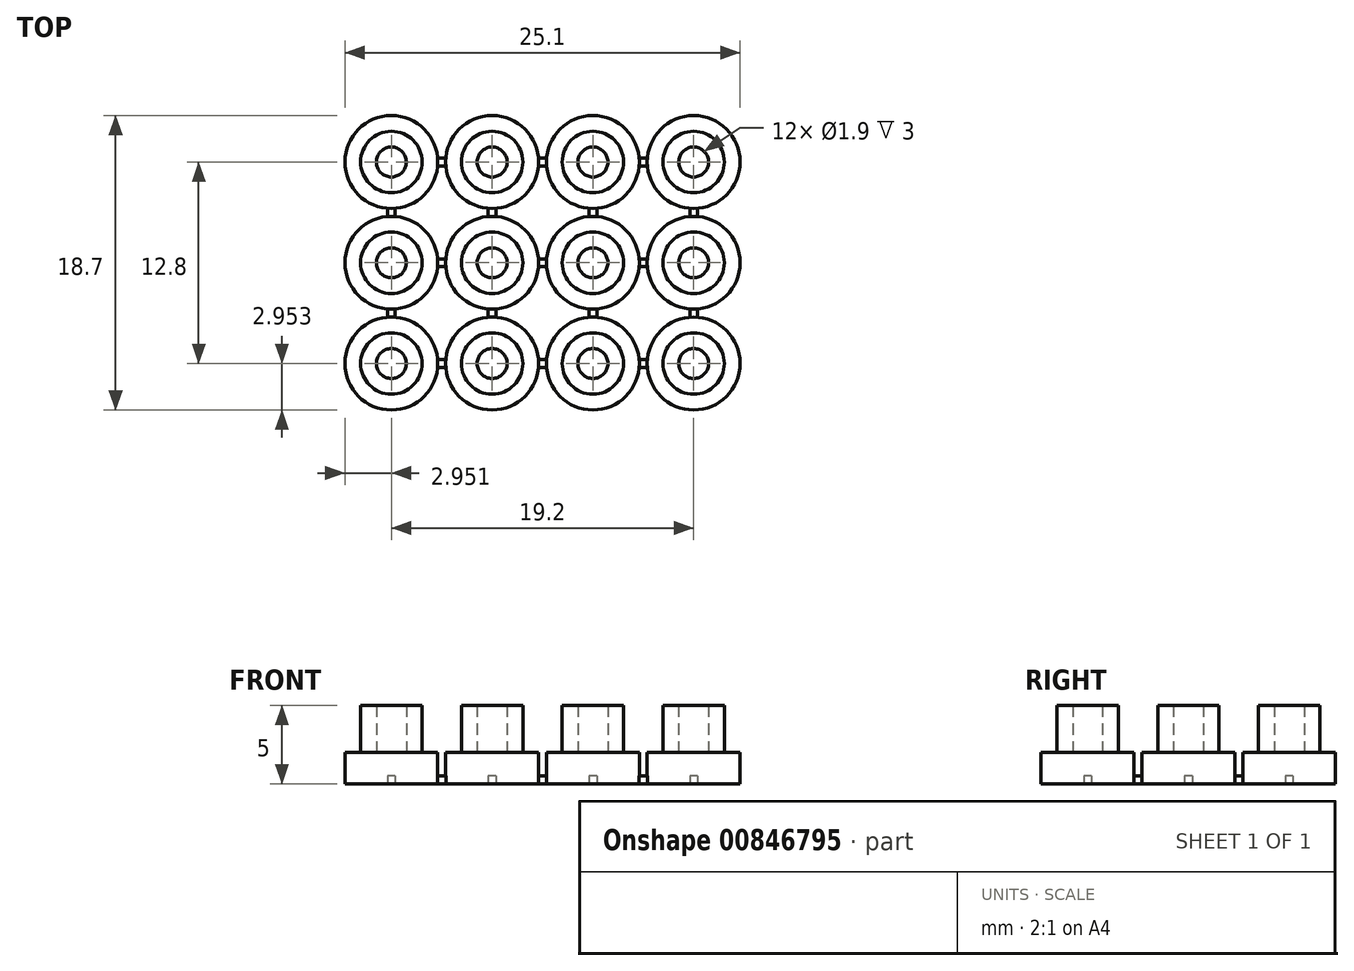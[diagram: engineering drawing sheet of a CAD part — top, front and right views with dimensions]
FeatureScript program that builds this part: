
annotation { "Feature Type Name" : "Feature", "Feature Type Description" : "" }
export const myFeature = defineFeature(function(context is Context, id is Id, definition is map)
    precondition{}
    {
        {
            var Q0;
            Q0=qCreatedBy(makeId("Top.planeOp"),FACE);
            var sketch = newSketch(context, id + "F0", { "sketchPlane" : qUnion([Q0])});
            skCircle(sketch, "E0", {"center": v(-49.05, 28.15) * mm, "radius": 0.95 * mm});
            skCircle(sketch, "E1", {"center": v(-49.05, 28.15) * mm, "radius": 1.95 * mm});
            skCircle(sketch, "E2", {"center": v(-49.05, 28.15) * mm, "radius": 2.95 * mm});
            skCircle(sketch, "E3.0.1.0", {"center": v(-49.05, 34.55) * mm, "radius": 2.95 * mm});
            skCircle(sketch, "E3.0.1.1", {"center": v(-49.05, 34.55) * mm, "radius": 1.95 * mm});
            skCircle(sketch, "E3.0.1.2", {"center": v(-49.05, 34.55) * mm, "radius": 0.95 * mm});
            skCircle(sketch, "E3.0.2.0", {"center": v(-49.05, 40.95) * mm, "radius": 2.95 * mm});
            skCircle(sketch, "E3.0.2.1", {"center": v(-49.05, 40.95) * mm, "radius": 1.95 * mm});
            skCircle(sketch, "E3.0.2.2", {"center": v(-49.05, 40.95) * mm, "radius": 0.95 * mm});
            skCircle(sketch, "E3.1.0.0", {"center": v(-42.65, 28.15) * mm, "radius": 2.95 * mm});
            skCircle(sketch, "E3.1.0.1", {"center": v(-42.65, 28.15) * mm, "radius": 1.95 * mm});
            skCircle(sketch, "E3.1.0.2", {"center": v(-42.65, 28.15) * mm, "radius": 0.95 * mm});
            skCircle(sketch, "E3.1.1.0", {"center": v(-42.65, 34.55) * mm, "radius": 2.95 * mm});
            skCircle(sketch, "E3.1.1.1", {"center": v(-42.65, 34.55) * mm, "radius": 1.95 * mm});
            skCircle(sketch, "E3.1.1.2", {"center": v(-42.65, 34.55) * mm, "radius": 0.95 * mm});
            skCircle(sketch, "E3.1.2.0", {"center": v(-42.65, 40.95) * mm, "radius": 2.95 * mm});
            skCircle(sketch, "E3.1.2.1", {"center": v(-42.65, 40.95) * mm, "radius": 1.95 * mm});
            skCircle(sketch, "E3.1.2.2", {"center": v(-42.65, 40.95) * mm, "radius": 0.95 * mm});
            skCircle(sketch, "E3.2.0.0", {"center": v(-36.25, 28.15) * mm, "radius": 2.95 * mm});
            skCircle(sketch, "E3.2.0.1", {"center": v(-36.25, 28.15) * mm, "radius": 1.95 * mm});
            skCircle(sketch, "E3.2.0.2", {"center": v(-36.25, 28.15) * mm, "radius": 0.95 * mm});
            skCircle(sketch, "E3.2.1.0", {"center": v(-36.25, 34.55) * mm, "radius": 2.95 * mm});
            skCircle(sketch, "E3.2.1.1", {"center": v(-36.25, 34.55) * mm, "radius": 1.95 * mm});
            skCircle(sketch, "E3.2.1.2", {"center": v(-36.25, 34.55) * mm, "radius": 0.95 * mm});
            skCircle(sketch, "E3.2.2.0", {"center": v(-36.25, 40.95) * mm, "radius": 2.95 * mm});
            skCircle(sketch, "E3.2.2.1", {"center": v(-36.25, 40.95) * mm, "radius": 1.95 * mm});
            skCircle(sketch, "E3.2.2.2", {"center": v(-36.25, 40.95) * mm, "radius": 0.95 * mm});
            skCircle(sketch, "E3.3.0.0", {"center": v(-29.85, 28.15) * mm, "radius": 2.95 * mm});
            skCircle(sketch, "E3.3.0.1", {"center": v(-29.85, 28.15) * mm, "radius": 1.95 * mm});
            skCircle(sketch, "E3.3.0.2", {"center": v(-29.85, 28.15) * mm, "radius": 0.95 * mm});
            skCircle(sketch, "E3.3.1.0", {"center": v(-29.85, 34.55) * mm, "radius": 2.95 * mm});
            skCircle(sketch, "E3.3.1.1", {"center": v(-29.85, 34.55) * mm, "radius": 1.95 * mm});
            skCircle(sketch, "E3.3.1.2", {"center": v(-29.85, 34.55) * mm, "radius": 0.95 * mm});
            skCircle(sketch, "E3.3.2.0", {"center": v(-29.85, 40.95) * mm, "radius": 2.95 * mm});
            skCircle(sketch, "E3.3.2.1", {"center": v(-29.85, 40.95) * mm, "radius": 1.95 * mm});
            skCircle(sketch, "E3.3.2.2", {"center": v(-29.85, 40.95) * mm, "radius": 0.95 * mm});
            skLineSegment(sketch, "E3.direction1", {"start": v(-49.05, 28.15) * mm, "end": v(-42.65, 28.15) * mm, "construction": true});
            skLineSegment(sketch, "E3.direction2", {"start": v(-49.05, 28.15) * mm, "end": v(-49.05, 34.55) * mm, "construction": true});
            skPoint(sketch, "E4", {"position": v(-49.05, 31.35) * mm});
            skPoint(sketch, "E5", {"position": v(-45.85, 28.15) * mm});
            skLineSegment(sketch, "E6.left", {"start": v(-48.8, 31.1) * mm, "end": v(-48.8, 31.61) * mm});
            skLineSegment(sketch, "E6.right", {"start": v(-49.3, 31.1) * mm, "end": v(-49.3, 31.61) * mm});
            skLineSegment(sketch, "E7.0.1.0", {"start": v(-49.3, 37.5) * mm, "end": v(-49.3, 38.01) * mm});
            skLineSegment(sketch, "E7.0.1.1", {"start": v(-48.8, 37.5) * mm, "end": v(-48.8, 38.01) * mm});
            skLineSegment(sketch, "E7.1.0.0", {"start": v(-42.9, 31.1) * mm, "end": v(-42.9, 31.61) * mm});
            skLineSegment(sketch, "E7.1.0.1", {"start": v(-42.4, 31.1) * mm, "end": v(-42.4, 31.61) * mm});
            skLineSegment(sketch, "E7.1.1.0", {"start": v(-42.9, 37.5) * mm, "end": v(-42.9, 38.01) * mm});
            skLineSegment(sketch, "E7.1.1.1", {"start": v(-42.4, 37.5) * mm, "end": v(-42.4, 38.01) * mm});
            skLineSegment(sketch, "E7.2.0.0", {"start": v(-36.5, 31.1) * mm, "end": v(-36.5, 31.61) * mm});
            skLineSegment(sketch, "E7.2.0.1", {"start": v(-36, 31.1) * mm, "end": v(-36, 31.61) * mm});
            skLineSegment(sketch, "E7.2.1.0", {"start": v(-36.5, 37.5) * mm, "end": v(-36.5, 38.01) * mm});
            skLineSegment(sketch, "E7.2.1.1", {"start": v(-36, 37.5) * mm, "end": v(-36, 38.01) * mm});
            skLineSegment(sketch, "E7.3.0.0", {"start": v(-30.1, 31.1) * mm, "end": v(-30.1, 31.61) * mm});
            skLineSegment(sketch, "E7.3.0.1", {"start": v(-29.6, 31.1) * mm, "end": v(-29.6, 31.61) * mm});
            skLineSegment(sketch, "E7.3.1.0", {"start": v(-30.1, 37.5) * mm, "end": v(-30.1, 38.01) * mm});
            skLineSegment(sketch, "E7.3.1.1", {"start": v(-29.6, 37.5) * mm, "end": v(-29.6, 38.01) * mm});
            skLineSegment(sketch, "E7.direction1", {"start": v(-49.3, 31.1) * mm, "end": v(-42.9, 31.1) * mm, "construction": true});
            skLineSegment(sketch, "E7.direction2", {"start": v(-49.3, 31.1) * mm, "end": v(-49.3, 37.5) * mm, "construction": true});
            skLineSegment(sketch, "E8.bottom", {"start": v(-45.59, 28.4) * mm, "end": v(-46.1, 28.4) * mm});
            skLineSegment(sketch, "E8.top", {"start": v(-45.59, 27.9) * mm, "end": v(-46.1, 27.9) * mm});
            skLineSegment(sketch, "E9.0.1.0", {"start": v(-45.59, 34.8) * mm, "end": v(-46.1, 34.8) * mm});
            skLineSegment(sketch, "E9.0.1.1", {"start": v(-45.59, 34.3) * mm, "end": v(-46.1, 34.3) * mm});
            skLineSegment(sketch, "E9.0.2.0", {"start": v(-45.59, 41.2) * mm, "end": v(-46.1, 41.2) * mm});
            skLineSegment(sketch, "E9.0.2.1", {"start": v(-45.59, 40.7) * mm, "end": v(-46.1, 40.7) * mm});
            skLineSegment(sketch, "E9.1.0.0", {"start": v(-39.19, 28.4) * mm, "end": v(-39.7, 28.4) * mm});
            skLineSegment(sketch, "E9.1.0.1", {"start": v(-39.19, 27.9) * mm, "end": v(-39.7, 27.9) * mm});
            skLineSegment(sketch, "E9.1.1.0", {"start": v(-39.19, 34.8) * mm, "end": v(-39.7, 34.8) * mm});
            skLineSegment(sketch, "E9.1.1.1", {"start": v(-39.19, 34.3) * mm, "end": v(-39.7, 34.3) * mm});
            skLineSegment(sketch, "E9.1.2.0", {"start": v(-39.19, 41.2) * mm, "end": v(-39.7, 41.2) * mm});
            skLineSegment(sketch, "E9.1.2.1", {"start": v(-39.19, 40.7) * mm, "end": v(-39.7, 40.7) * mm});
            skLineSegment(sketch, "E9.2.0.0", {"start": v(-32.79, 28.4) * mm, "end": v(-33.3, 28.4) * mm});
            skLineSegment(sketch, "E9.2.0.1", {"start": v(-32.79, 27.9) * mm, "end": v(-33.3, 27.9) * mm});
            skLineSegment(sketch, "E9.2.1.0", {"start": v(-32.79, 34.8) * mm, "end": v(-33.3, 34.8) * mm});
            skLineSegment(sketch, "E9.2.1.1", {"start": v(-32.79, 34.3) * mm, "end": v(-33.3, 34.3) * mm});
            skLineSegment(sketch, "E9.2.2.0", {"start": v(-32.79, 41.2) * mm, "end": v(-33.3, 41.2) * mm});
            skLineSegment(sketch, "E9.2.2.1", {"start": v(-32.79, 40.7) * mm, "end": v(-33.3, 40.7) * mm});
            skLineSegment(sketch, "E9.direction1", {"start": v(-46.1, 27.9) * mm, "end": v(-39.7, 27.9) * mm, "construction": true});
            skLineSegment(sketch, "E9.direction2", {"start": v(-46.1, 27.9) * mm, "end": v(-46.1, 34.3) * mm, "construction": true});
            skSolve(sketch);
        }
        {
            var Q0;
            Q0=makeQuery(id+"F0.imprint","IMPRINT",FACE,{"disambiguationData":[TD([[makeQuery(id+"F0.imprint","IMPRINT",EDGE,{"derivedFrom":sQuery(id+"F0.wireOp",EDGE,"E0")}),-1.0]])]});
            var Q1;
            Q1=makeQuery(id+"F0.imprint","IMPRINT",FACE,{"disambiguationData":[TD([[makeQuery(id+"F0.imprint","IMPRINT",EDGE,{"derivedFrom":sQuery(id+"F0.wireOp",EDGE,"E3.1.0.1")}),1.0]])]});
            var Q2;
            Q2=makeQuery(id+"F0.imprint","IMPRINT",FACE,{"disambiguationData":[TD([[makeQuery(id+"F0.imprint","IMPRINT",EDGE,{"derivedFrom":sQuery(id+"F0.wireOp",EDGE,"E3.2.0.1")}),1.0]])]});
            var Q3;
            Q3=makeQuery(id+"F0.imprint","IMPRINT",FACE,{"disambiguationData":[TD([[makeQuery(id+"F0.imprint","IMPRINT",EDGE,{"derivedFrom":sQuery(id+"F0.wireOp",EDGE,"E3.0.1.1")}),1.0]])]});
            var Q4;
            Q4=makeQuery(id+"F0.imprint","IMPRINT",FACE,{"disambiguationData":[TD([[makeQuery(id+"F0.imprint","IMPRINT",EDGE,{"derivedFrom":sQuery(id+"F0.wireOp",EDGE,"E3.0.2.1")}),1.0]])]});
            var Q5;
            Q5=makeQuery(id+"F0.imprint","IMPRINT",FACE,{"disambiguationData":[TD([[makeQuery(id+"F0.imprint","IMPRINT",EDGE,{"derivedFrom":sQuery(id+"F0.wireOp",EDGE,"E3.1.1.1")}),1.0]])]});
            var Q6;
            Q6=makeQuery(id+"F0.imprint","IMPRINT",FACE,{"disambiguationData":[TD([[makeQuery(id+"F0.imprint","IMPRINT",EDGE,{"derivedFrom":sQuery(id+"F0.wireOp",EDGE,"E3.1.2.1")}),1.0]])]});
            var Q7;
            Q7=makeQuery(id+"F0.imprint","IMPRINT",FACE,{"disambiguationData":[TD([[makeQuery(id+"F0.imprint","IMPRINT",EDGE,{"derivedFrom":sQuery(id+"F0.wireOp",EDGE,"E3.2.1.1")}),1.0]])]});
            var Q8;
            Q8=makeQuery(id+"F0.imprint","IMPRINT",FACE,{"disambiguationData":[TD([[makeQuery(id+"F0.imprint","IMPRINT",EDGE,{"derivedFrom":sQuery(id+"F0.wireOp",EDGE,"E3.2.2.1")}),1.0]])]});
            var Q9;
            Q9=makeQuery(id+"F0.imprint","IMPRINT",FACE,{"disambiguationData":[TD([[makeQuery(id+"F0.imprint","IMPRINT",EDGE,{"derivedFrom":sQuery(id+"F0.wireOp",EDGE,"E3.3.2.1")}),1.0]])]});
            var Q10;
            Q10=makeQuery(id+"F0.imprint","IMPRINT",FACE,{"disambiguationData":[TD([[makeQuery(id+"F0.imprint","IMPRINT",EDGE,{"derivedFrom":sQuery(id+"F0.wireOp",EDGE,"E3.3.1.1")}),1.0]])]});
            var Q11;
            Q11=makeQuery(id+"F0.imprint","IMPRINT",FACE,{"disambiguationData":[TD([[makeQuery(id+"F0.imprint","IMPRINT",EDGE,{"derivedFrom":sQuery(id+"F0.wireOp",EDGE,"E3.3.0.1")}),1.0]])]});
            extrude(context, id + "F1", {"entities" : qUnion([Q0, Q1, Q2, Q3, Q4, Q5, Q6, Q7, Q8, Q9, Q10, Q11]), "depth" : 5 * mm, "offsetDistance" : 25 * mm});
        }
        {
            var Q0;
            Q0=makeQuery(id+"F0.imprint","IMPRINT",FACE,{"disambiguationData":[TD([[makeQuery(id+"F0.imprint","IMPRINT",EDGE,{"derivedFrom":sQuery(id+"F0.wireOp",EDGE,"E1")}),-1.0]])]});
            var Q1;
            Q1=makeQuery(id+"F0.imprint","IMPRINT",FACE,{"disambiguationData":[TD([[makeQuery(id+"F0.imprint","IMPRINT",EDGE,{"derivedFrom":sQuery(id+"F0.wireOp",EDGE,"E0")}),1.0]])]});
            var Q2;
            Q2=makeQuery(id+"F0.imprint","IMPRINT",FACE,{"disambiguationData":[TD([[makeQuery(id+"F0.imprint","IMPRINT",EDGE,{"derivedFrom":sQuery(id+"F0.wireOp",EDGE,"E3.0.1.0")}),1.0]])]});
            var Q3;
            Q3=makeQuery(id+"F0.imprint","IMPRINT",FACE,{"disambiguationData":[TD([[makeQuery(id+"F0.imprint","IMPRINT",EDGE,{"derivedFrom":sQuery(id+"F0.wireOp",EDGE,"E3.0.1.2")}),1.0]])]});
            var Q4;
            Q4=makeQuery(id+"F0.imprint","IMPRINT",FACE,{"disambiguationData":[TD([[makeQuery(id+"F0.imprint","IMPRINT",EDGE,{"derivedFrom":sQuery(id+"F0.wireOp",EDGE,"E3.0.2.0")}),1.0]])]});
            var Q5;
            Q5=makeQuery(id+"F0.imprint","IMPRINT",FACE,{"disambiguationData":[TD([[makeQuery(id+"F0.imprint","IMPRINT",EDGE,{"derivedFrom":sQuery(id+"F0.wireOp",EDGE,"E3.0.2.2")}),1.0]])]});
            var Q6;
            Q6=makeQuery(id+"F0.imprint","IMPRINT",FACE,{"disambiguationData":[TD([[makeQuery(id+"F0.imprint","IMPRINT",EDGE,{"derivedFrom":sQuery(id+"F0.wireOp",EDGE,"E3.1.2.0")}),1.0]])]});
            var Q7;
            Q7=makeQuery(id+"F0.imprint","IMPRINT",FACE,{"disambiguationData":[TD([[makeQuery(id+"F0.imprint","IMPRINT",EDGE,{"derivedFrom":sQuery(id+"F0.wireOp",EDGE,"E3.1.2.2")}),1.0]])]});
            var Q8;
            Q8=makeQuery(id+"F0.imprint","IMPRINT",FACE,{"disambiguationData":[TD([[makeQuery(id+"F0.imprint","IMPRINT",EDGE,{"derivedFrom":sQuery(id+"F0.wireOp",EDGE,"E3.1.1.0")}),1.0]])]});
            var Q9;
            Q9=makeQuery(id+"F0.imprint","IMPRINT",FACE,{"disambiguationData":[TD([[makeQuery(id+"F0.imprint","IMPRINT",EDGE,{"derivedFrom":sQuery(id+"F0.wireOp",EDGE,"E3.1.1.2")}),1.0]])]});
            var Q10;
            Q10=makeQuery(id+"F0.imprint","IMPRINT",FACE,{"disambiguationData":[TD([[makeQuery(id+"F0.imprint","IMPRINT",EDGE,{"derivedFrom":sQuery(id+"F0.wireOp",EDGE,"E3.1.0.0")}),1.0]])]});
            var Q11;
            Q11=makeQuery(id+"F0.imprint","IMPRINT",FACE,{"disambiguationData":[TD([[makeQuery(id+"F0.imprint","IMPRINT",EDGE,{"derivedFrom":sQuery(id+"F0.wireOp",EDGE,"E3.1.0.2")}),1.0]])]});
            var Q12;
            Q12=makeQuery(id+"F0.imprint","IMPRINT",FACE,{"disambiguationData":[TD([[makeQuery(id+"F0.imprint","IMPRINT",EDGE,{"derivedFrom":sQuery(id+"F0.wireOp",EDGE,"E3.2.0.0")}),1.0]])]});
            var Q13;
            Q13=makeQuery(id+"F0.imprint","IMPRINT",FACE,{"disambiguationData":[TD([[makeQuery(id+"F0.imprint","IMPRINT",EDGE,{"derivedFrom":sQuery(id+"F0.wireOp",EDGE,"E3.2.0.2")}),1.0]])]});
            var Q14;
            Q14=makeQuery(id+"F0.imprint","IMPRINT",FACE,{"disambiguationData":[TD([[makeQuery(id+"F0.imprint","IMPRINT",EDGE,{"derivedFrom":sQuery(id+"F0.wireOp",EDGE,"E3.2.1.0")}),1.0]])]});
            var Q15;
            Q15=makeQuery(id+"F0.imprint","IMPRINT",FACE,{"disambiguationData":[TD([[makeQuery(id+"F0.imprint","IMPRINT",EDGE,{"derivedFrom":sQuery(id+"F0.wireOp",EDGE,"E3.2.1.2")}),1.0]])]});
            var Q16;
            Q16=makeQuery(id+"F0.imprint","IMPRINT",FACE,{"disambiguationData":[TD([[makeQuery(id+"F0.imprint","IMPRINT",EDGE,{"derivedFrom":sQuery(id+"F0.wireOp",EDGE,"E3.2.2.0")}),1.0]])]});
            var Q17;
            Q17=makeQuery(id+"F0.imprint","IMPRINT",FACE,{"disambiguationData":[TD([[makeQuery(id+"F0.imprint","IMPRINT",EDGE,{"derivedFrom":sQuery(id+"F0.wireOp",EDGE,"E3.2.2.2")}),1.0]])]});
            var Q18;
            Q18=makeQuery(id+"F0.imprint","IMPRINT",FACE,{"disambiguationData":[TD([[makeQuery(id+"F0.imprint","IMPRINT",EDGE,{"derivedFrom":sQuery(id+"F0.wireOp",EDGE,"E3.3.2.0")}),1.0]])]});
            var Q19;
            Q19=makeQuery(id+"F0.imprint","IMPRINT",FACE,{"disambiguationData":[TD([[makeQuery(id+"F0.imprint","IMPRINT",EDGE,{"derivedFrom":sQuery(id+"F0.wireOp",EDGE,"E3.3.2.2")}),1.0]])]});
            var Q20;
            Q20=makeQuery(id+"F0.imprint","IMPRINT",FACE,{"disambiguationData":[TD([[makeQuery(id+"F0.imprint","IMPRINT",EDGE,{"derivedFrom":sQuery(id+"F0.wireOp",EDGE,"E3.3.1.0")}),1.0]])]});
            var Q21;
            Q21=makeQuery(id+"F0.imprint","IMPRINT",FACE,{"disambiguationData":[TD([[makeQuery(id+"F0.imprint","IMPRINT",EDGE,{"derivedFrom":sQuery(id+"F0.wireOp",EDGE,"E3.3.1.2")}),1.0]])]});
            var Q22;
            Q22=makeQuery(id+"F0.imprint","IMPRINT",FACE,{"disambiguationData":[TD([[makeQuery(id+"F0.imprint","IMPRINT",EDGE,{"derivedFrom":sQuery(id+"F0.wireOp",EDGE,"E3.3.0.0")}),1.0]])]});
            var Q23;
            Q23=makeQuery(id+"F0.imprint","IMPRINT",FACE,{"disambiguationData":[TD([[makeQuery(id+"F0.imprint","IMPRINT",EDGE,{"derivedFrom":sQuery(id+"F0.wireOp",EDGE,"E3.3.0.2")}),1.0]])]});
            extrude(context, id + "F2", {"entities" : qUnion([Q0, Q1, Q2, Q3, Q4, Q5, Q6, Q7, Q8, Q9, Q10, Q11, Q12, Q13, Q14, Q15, Q16, Q17, Q18, Q19, Q20, Q21, Q22, Q23]), "operationType" : NewBodyOperationType.ADD, "depth" : 2 * mm, "offsetDistance" : 25 * mm});
        }
        {
            var Q0;
            {var subQ0=sQuery(id+"F0.wireOp",EDGE,"E8.bottom");Q0=makeQuery(id+"F0.imprint","IMPRINT",FACE,{"disambiguationData":[TD([[makeQuery(id+"F0.imprint","IMPRINT",EDGE,{"derivedFrom":subQ0}),1.0]])]});}
            var Q1;
            {var subQ0=sQuery(id+"F0.wireOp",EDGE,"E9.1.0.0");Q1=makeQuery(id+"F0.imprint","IMPRINT",FACE,{"disambiguationData":[TD([[makeQuery(id+"F0.imprint","IMPRINT",EDGE,{"derivedFrom":subQ0}),1.0]])]});}
            var Q2;
            {var subQ0=sQuery(id+"F0.wireOp",EDGE,"E9.2.0.0");Q2=makeQuery(id+"F0.imprint","IMPRINT",FACE,{"disambiguationData":[TD([[makeQuery(id+"F0.imprint","IMPRINT",EDGE,{"derivedFrom":subQ0}),1.0]])]});}
            var Q3;
            {var subQ0=sQuery(id+"F0.wireOp",EDGE,"E9.2.1.0");Q3=makeQuery(id+"F0.imprint","IMPRINT",FACE,{"disambiguationData":[TD([[makeQuery(id+"F0.imprint","IMPRINT",EDGE,{"derivedFrom":subQ0}),1.0]])]});}
            var Q4;
            {var subQ0=sQuery(id+"F0.wireOp",EDGE,"E7.3.0.0");Q4=makeQuery(id+"F0.imprint","IMPRINT",FACE,{"disambiguationData":[TD([[makeQuery(id+"F0.imprint","IMPRINT",EDGE,{"derivedFrom":subQ0}),-1.0]])]});}
            var Q5;
            {var subQ0=sQuery(id+"F0.wireOp",EDGE,"E7.2.0.0");Q5=makeQuery(id+"F0.imprint","IMPRINT",FACE,{"disambiguationData":[TD([[makeQuery(id+"F0.imprint","IMPRINT",EDGE,{"derivedFrom":subQ0}),-1.0]])]});}
            var Q6;
            {var subQ0=sQuery(id+"F0.wireOp",EDGE,"E7.1.0.0");Q6=makeQuery(id+"F0.imprint","IMPRINT",FACE,{"disambiguationData":[TD([[makeQuery(id+"F0.imprint","IMPRINT",EDGE,{"derivedFrom":subQ0}),-1.0]])]});}
            var Q7;
            {var subQ0=sQuery(id+"F0.wireOp",EDGE,"E6.left");Q7=makeQuery(id+"F0.imprint","IMPRINT",FACE,{"disambiguationData":[TD([[makeQuery(id+"F0.imprint","IMPRINT",EDGE,{"derivedFrom":subQ0}),1.0]])]});}
            var Q8;
            {var subQ0=sQuery(id+"F0.wireOp",EDGE,"E7.0.1.0");Q8=makeQuery(id+"F0.imprint","IMPRINT",FACE,{"disambiguationData":[TD([[makeQuery(id+"F0.imprint","IMPRINT",EDGE,{"derivedFrom":subQ0}),-1.0]])]});}
            var Q9;
            {var subQ0=sQuery(id+"F0.wireOp",EDGE,"E7.1.1.0");Q9=makeQuery(id+"F0.imprint","IMPRINT",FACE,{"disambiguationData":[TD([[makeQuery(id+"F0.imprint","IMPRINT",EDGE,{"derivedFrom":subQ0}),-1.0]])]});}
            var Q10;
            {var subQ0=sQuery(id+"F0.wireOp",EDGE,"E9.0.2.0");Q10=makeQuery(id+"F0.imprint","IMPRINT",FACE,{"disambiguationData":[TD([[makeQuery(id+"F0.imprint","IMPRINT",EDGE,{"derivedFrom":subQ0}),1.0]])]});}
            var Q11;
            {var subQ0=sQuery(id+"F0.wireOp",EDGE,"E9.0.1.0");Q11=makeQuery(id+"F0.imprint","IMPRINT",FACE,{"disambiguationData":[TD([[makeQuery(id+"F0.imprint","IMPRINT",EDGE,{"derivedFrom":subQ0}),1.0]])]});}
            var Q12;
            {var subQ0=sQuery(id+"F0.wireOp",EDGE,"E9.1.1.0");Q12=makeQuery(id+"F0.imprint","IMPRINT",FACE,{"disambiguationData":[TD([[makeQuery(id+"F0.imprint","IMPRINT",EDGE,{"derivedFrom":subQ0}),1.0]])]});}
            var Q13;
            {var subQ0=sQuery(id+"F0.wireOp",EDGE,"E9.1.2.0");Q13=makeQuery(id+"F0.imprint","IMPRINT",FACE,{"disambiguationData":[TD([[makeQuery(id+"F0.imprint","IMPRINT",EDGE,{"derivedFrom":subQ0}),1.0]])]});}
            var Q14;
            {var subQ0=sQuery(id+"F0.wireOp",EDGE,"E7.2.1.0");Q14=makeQuery(id+"F0.imprint","IMPRINT",FACE,{"disambiguationData":[TD([[makeQuery(id+"F0.imprint","IMPRINT",EDGE,{"derivedFrom":subQ0}),-1.0]])]});}
            var Q15;
            {var subQ0=sQuery(id+"F0.wireOp",EDGE,"E9.2.2.0");Q15=makeQuery(id+"F0.imprint","IMPRINT",FACE,{"disambiguationData":[TD([[makeQuery(id+"F0.imprint","IMPRINT",EDGE,{"derivedFrom":subQ0}),1.0]])]});}
            var Q16;
            {var subQ0=sQuery(id+"F0.wireOp",EDGE,"E7.3.1.0");Q16=makeQuery(id+"F0.imprint","IMPRINT",FACE,{"disambiguationData":[TD([[makeQuery(id+"F0.imprint","IMPRINT",EDGE,{"derivedFrom":subQ0}),-1.0]])]});}
            extrude(context, id + "F3", {"entities" : qUnion([Q0, Q1, Q2, Q3, Q4, Q5, Q6, Q7, Q8, Q9, Q10, Q11, Q12, Q13, Q14, Q15, Q16]), "depth" : 0.5 * mm, "offsetDistance" : 25 * mm});
        }
    });
